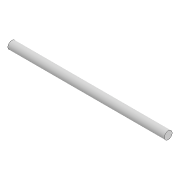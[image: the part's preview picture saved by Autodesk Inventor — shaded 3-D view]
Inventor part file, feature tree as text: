
AUTODESK INVENTOR PART (.ipt)
format: ipt  version: 2022 (Build 260153000, 153)  size: 71,680 bytes
history: native  units: mm
features: extrude x1, sketch x1
ambient origin geometry x8: Origin, YZ Plane, XZ Plane, XY Plane, X Axis, Y Axis, Z Axis, Center Point
bodies: Solid1 (feature_tree)
feature tree (2):
  extrude  "Extrusion1"  Depth=100.0mm TaperAngle=0.0deg
  sketch  "Sketch1"  dims[d0=5.0mm d1=100.0mm d2=0.0mm]
